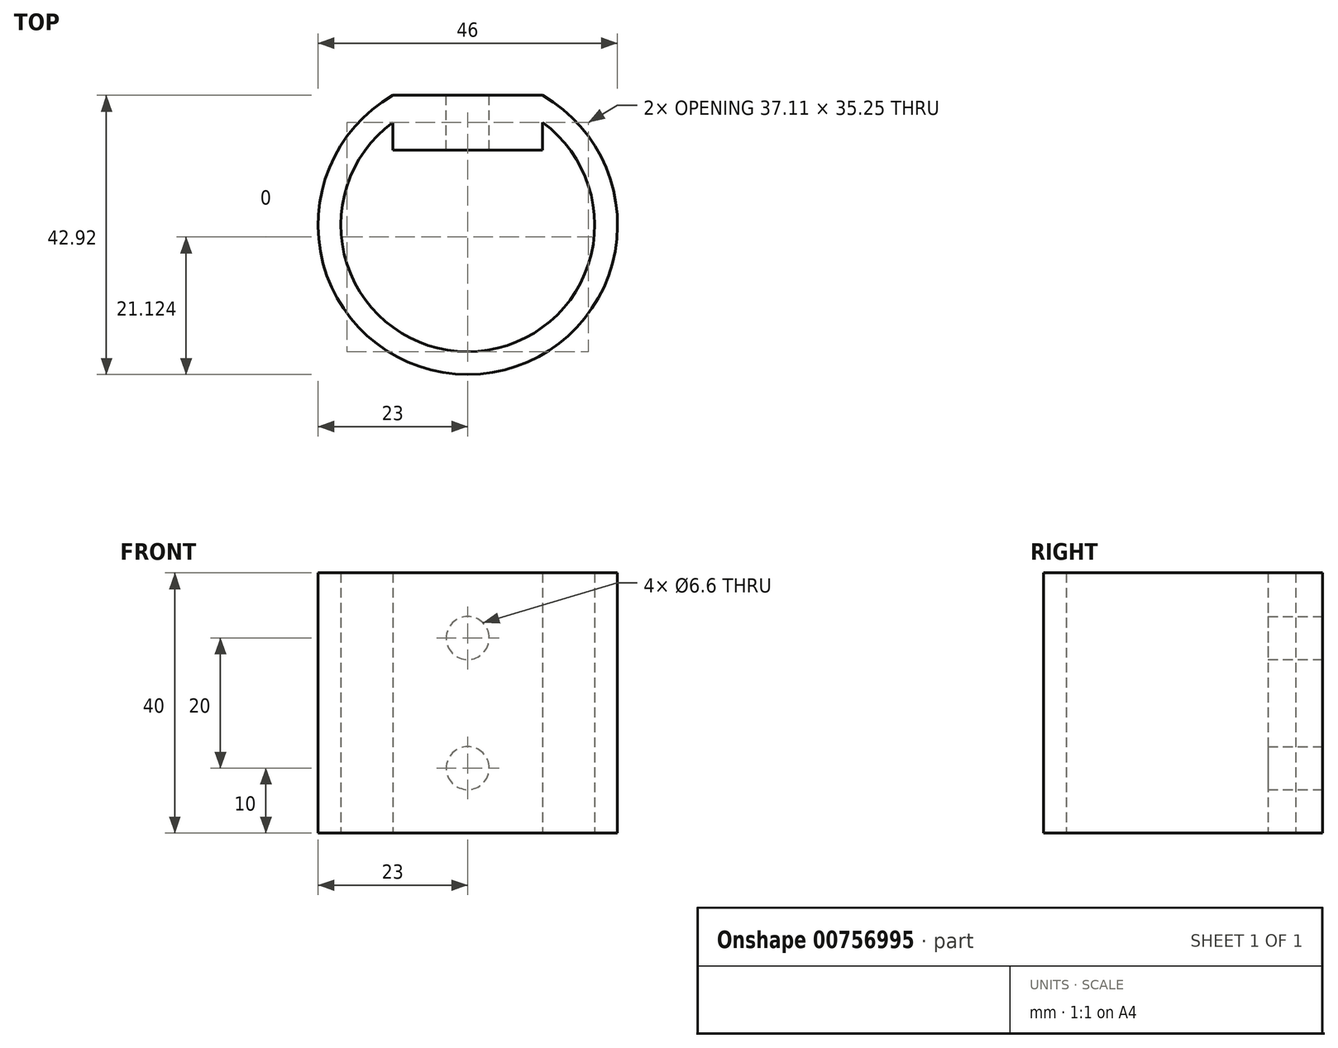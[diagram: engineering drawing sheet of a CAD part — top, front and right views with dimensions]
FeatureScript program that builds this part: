
annotation { "Feature Type Name" : "Feature", "Feature Type Description" : "" }
export const myFeature = defineFeature(function(context is Context, id is Id, definition is map)
    precondition{}
    {
        {
            var Q0;
            Q0=qCreatedBy(makeId("Top.planeOp"),FACE);
            var sketch = newSketch(context, id + "F0", { "sketchPlane" : qUnion([Q0])});
            skArc(sketch, "E0", {"start": v(-11.5, 19.92) * mm, "mid": v(0, -23) * mm, "end": v(11.5, 19.92) * mm});
            skArc(sketch, "E1", {"start": v(-11.5, 15.75) * mm, "mid": v(0, -19.5) * mm, "end": v(11.5, 15.75) * mm});
            skLineSegment(sketch, "E2", {"start": v(-11.5, 15.75) * mm, "end": v(-11.5, 11.5) * mm});
            skLineSegment(sketch, "E3", {"start": v(-11.5, 11.5) * mm, "end": v(11.5, 11.5) * mm});
            skLineSegment(sketch, "E4", {"start": v(11.5, 11.5) * mm, "end": v(11.5, 15.75) * mm});
            skLineSegment(sketch, "E5", {"start": v(-11.5, 19.92) * mm, "end": v(11.5, 19.92) * mm});
            skSolve(sketch);
        }
        {
            var Q0;
            Q0=makeQuery(id+"F0.imprint","IMPRINT",FACE,{"disambiguationData":[TD([[makeQuery(id+"F0.imprint","IMPRINT",EDGE,{"derivedFrom":sQuery(id+"F0.wireOp",EDGE,"E0")}),1.0]])]});
            extrude(context, id + "F1", {"entities" : qUnion([Q0]), "depth" : 40 * mm, "offsetDistance" : 25 * mm});
        }
        {
            var Q0;
            Q0=makeQuery(id+"F1.opExtrude","SWEPT_FACE",FACE,{"disambiguationData":[OSD([sQuery(id+"F0.wireOp",EDGE,"E5")])]});
            var sketch = newSketch(context, id + "F2", { "sketchPlane" : qUnion([Q0])});
            skCircle(sketch, "E6", {"center": v(0, 30) * mm, "radius": 3.3 * mm});
            skCircle(sketch, "E7", {"center": v(0, 10) * mm, "radius": 3.3 * mm});
            skLineSegment(sketch, "E8", {"start": v(0, 30) * mm, "end": v(0, 10) * mm, "construction": true});
            skSolve(sketch);
        }
        {
            var Q0;
            Q0=makeQuery(id+"F2.imprint","IMPRINT",FACE,{"disambiguationData":[TD([[makeQuery(id+"F2.imprint","IMPRINT",EDGE,{"derivedFrom":sQuery(id+"F2.wireOp",EDGE,"E6")}),1.0]])]});
            var Q1;
            Q1=makeQuery(id+"F2.imprint","IMPRINT",FACE,{"disambiguationData":[TD([[makeQuery(id+"F2.imprint","IMPRINT",EDGE,{"derivedFrom":sQuery(id+"F2.wireOp",EDGE,"E7")}),1.0]])]});
            extrude(context, id + "F3", {"entities" : qUnion([Q0, Q1]), "operationType" : NewBodyOperationType.REMOVE, "endBound" : BoundingType.UP_TO_NEXT, "oppositeDirection" : true, "depth" : 25 * mm, "offsetDistance" : 25 * mm});
        }
    });
